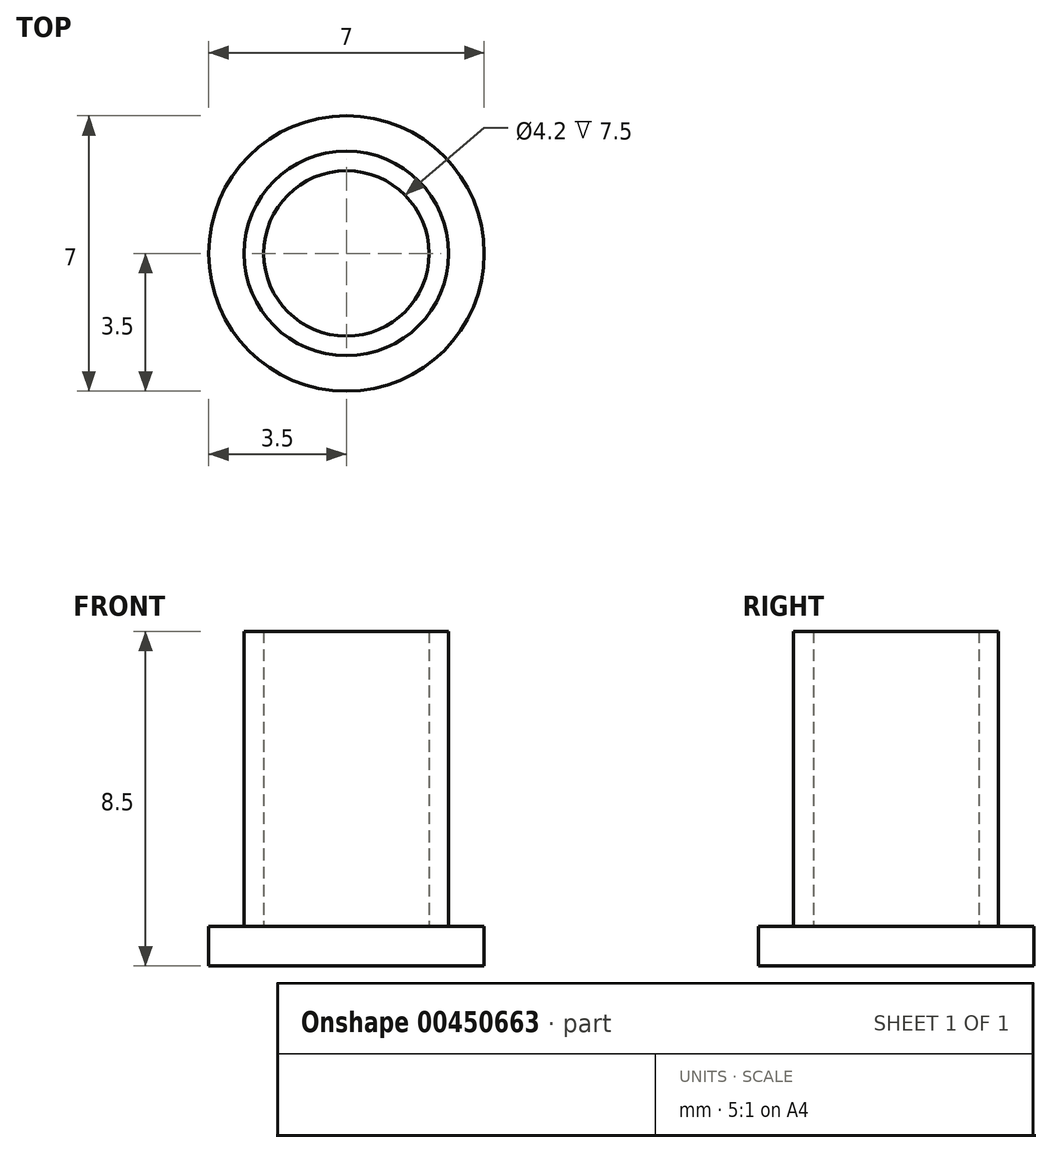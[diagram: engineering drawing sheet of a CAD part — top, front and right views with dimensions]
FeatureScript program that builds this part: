
annotation { "Feature Type Name" : "Feature", "Feature Type Description" : "" }
export const myFeature = defineFeature(function(context is Context, id is Id, definition is map)
    precondition{}
    {
        {
            var Q0;
            Q0=qCreatedBy(makeId("Top.planeOp"),FACE);
            var sketch = newSketch(context, id + "F0", { "sketchPlane" : qUnion([Q0])});
            skCircle(sketch, "E0", {"center": v(0, 0) * mm, "radius": 3.5 * mm});
            skSolve(sketch);
        }
        {
            var Q0;
            Q0=qSketchRegion(id+"F0",true);
            extrude(context, id + "F1", {"entities" : qUnion([Q0]), "endBound" : BoundingType.SYMMETRIC, "depth" : 1 * mm});
        }
        {
            var Q0;
            Q0=makeQuery(id+"F1.opExtrude","CAP_FACE",FACE,{"disambiguationData":[OSD([sQuery(id+"F0.wireOp",EDGE,"E0")])],"isStart":false});
            var sketch = newSketch(context, id + "F2", { "sketchPlane" : qUnion([Q0])});
            skCircle(sketch, "E1", {"center": v(0, 0) * mm, "radius": 2.6 * mm});
            skCircle(sketch, "E2", {"center": v(0, 0) * mm, "radius": 2.1 * mm});
            skSolve(sketch);
        }
        {
            var Q0;
            Q0=qSketchRegion(id+"F2",true);
            extrude(context, id + "F3", {"entities" : qUnion([Q0]), "operationType" : NewBodyOperationType.ADD, "depth" : 7.5 * mm});
        }
    });
